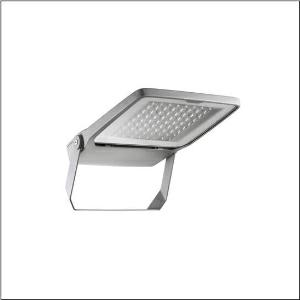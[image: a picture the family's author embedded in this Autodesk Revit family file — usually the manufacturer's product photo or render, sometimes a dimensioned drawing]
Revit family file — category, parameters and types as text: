
# Revit family: floodlight_fl_20_mini___rs17_5xa7672c2b1ac_f498
name_source: partatom
category: Lighting Fixtures
units: mm (PartAtom-declared; Revit-internal decimal feet)

## family parameters
Cut with Voids When Loaded = No
Host = Face
Light Source = No
Part Type = Normal
Room Calculation Point = No
Round Connector Dimension = Use Diameter
Shared = No

## types (1)
- --- (1 x LED 4000K / CRI = 70 (unbekannt), 13350 lm, 4000K)
    Apparent Load = 96 VA
    CIE Flux Codes = 79 92 99 100 100
    Color Rendering = 70
    Color Temperature = 4000K
    Default Elevation = 1800 mm
    Description = Floodlight FL 20 mini, floodlight, primary light control with lens, of plastic, primary optical cover: protective disc, of toughened safety glass, transparent, light distribution: RS17, light emission: direct distribution, primary light characteristic: rotationally symmetric, installation type: surface-mounted, LED, High Power LED, rated luminous flux: 13.350lm, luminous efficacy: 139lm/W, light colour: 740, colour temperature: 4000K, control gear: ECG Plus, control: flexible luminous flux parameterisation, time-dependent luminous flux control, digital communication interface, power reduction, overheat protection, electronic power reduction, with terminal, 5-pole, max. 2.5mm², mains connection: 220..240V, AC, 50/60Hz, rated input power: 96W, LED unit, of diecast aluminium, powder-coated, Siteco® metallic grey (DB 702S), corrosivity category C5 mid according to DIN EN ISO 12944, incl. 1x M20 cable gland for cable Ø 6.5..12mm, length: 446mm, width: 355mm, height: 62mm, housing frame, of diecast aluminium, powder-coated, Siteco® metallic grey (DB 702S), mounting bracket, of steel, powder-coated, Siteco® metallic grey (DB 702S), DALI, protection rating (complete): IP66, insulation class (complete): insulation class II (safety insulation), certification: CE, ENEC, VDE, protection symbol: D, permissible operating ambient temperature: -40..+40°C, permissible operating ambient temperature for outdoor applications: -40..+50°C, standard: DIN EN 12944, packaging unit: 1 piece

Light Distribution: RS17
    Height = 62 mm
    Lamp = 1 x LED 4000K / CRI >= 70 (unbekannt)
    Lamp Light Flux = 13350 lm
    Lamp count = 1
    Length = 467 mm
    Luminous efficacy = 139 lm/W
    Manufacturer = Siteco
    ModVariant = No
    Model = 5XA7672C2B1AC
    Mounting Place = Wall
    Mounting Type = Surface mounted
    Number of Poles = 1
    OnlyDefault = Yes
    Power Factor = 1
    Product Name = Floodlight FL 20 mini | RS17
    Product group = floodlight | wall mounted
    ProductGroupID = 2001
    Protection Class = Protection class II
    Protection Degree = IP 66
    RLX_Detail_Level = 1
    RLX_Emergency_Light_Flux = 0 lm
    RLX_Emergency_Type = 0
    RLX_Emergency_Type_DB = No
    RlxData = <blob elided: 68989 chars, md5=67283423>
    Socket = socket
    Standby Power = 0 W
    System Light Flux = 13350 lm
    System Power = 96 W
    Type Comments = factory setting: luminous flux: 100 % | dim-lin: 254 | 500 mA
    Type Image = l_1005948.jpg
    URL = http://relux.com
    VarID = @adj_163013
    Voltage = 0 V
    Weight = 0.00 kg
    Width = 335 mm

## geometry (parser evidence)
native form markers: Blend x4, Sweep x13
no freeform markers — native parametric forms only
